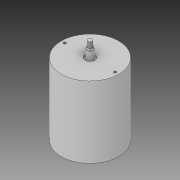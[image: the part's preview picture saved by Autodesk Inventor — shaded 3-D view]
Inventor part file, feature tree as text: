
AUTODESK INVENTOR PART (.ipt)
format: ipt  version: 2019 (Build 230136000, 136)  size: 122,368 bytes
history: native  units: mm
features: sketch x7, extrude x5, hole x2, thread x1
ambient origin geometry x8: Origin, YZ Plane, XZ Plane, XY Plane, X Axis, Y Axis, Z Axis, Center Point
bodies: Solid1 (feature_tree)
feature tree (15):
  extrude  "Extrusion1"  Depth=134.0mm TaperAngle=0.0deg
  extrude  "Extrusion2"  Depth=2.5mm TaperAngle=0.0deg
  extrude  "Extrusion3"  Depth=17.0mm TaperAngle=0.0deg
  extrude  "Extrusion4"  Depth=8.5mm
  hole  "Hole1"  [1 undecoded]
  hole  "Hole2"  [1 undecoded]
  extrude  "Extrusion5"  Depth=10.0mm
  thread  "Thread1"  [1 undecoded]
  sketch  "Sketch1"  dims[d0=108.0mm d1=134.0mm d2=0.0mm]
  sketch  "Sketch2"  dims[d3=18.0mm d4=2.5mm d5=0.0mm]
  sketch  "Sketch3"  dims[d6=12.0mm d7=17.0mm d8=0.0mm]
  sketch  "Sketch4"  dims[d9=10.0mm d10=8.5mm]
  sketch  "Sketch5"  dims[d11=3.5mm d12=0.0mm d16=94.5mm]
  sketch  "Sketch6"  dims[d17=4.917mm d18=10.0mm d19=4.0mm d20=2.0mm d21=90.0deg d22=10.0mm d23=20.594885mm d24=94.5mm]
  sketch  "Sketch7"  dims[d25=4.917mm d26=10.0mm d27=4.0mm d28=2.0mm d29=90.0deg d30=10.0mm d31=20.594885mm d32=8.0mm d33=10.5mm d34=0.0mm d35=10.0mm d36=0.0mm]
note: 3 required parameter values undecoded (feature->parameter linkage not recoverable at this tier; creation-order binding heuristic only, values carry confidence <= 0.55)
